# Revit family: Casement_34_B_Top_Hung_Standard
name_source: partatom
category: Windows
revit_build: Autodesk Revit 2014 (Build: 20130308_1515(x64)
units: mm (PartAtom-declared; Revit-internal decimal feet)

## types (6) — shared parameters
Aluminium Thickness = 1 mm  [stored 0.00328084 ft]
Area Pane Left = 0.23 m²
Bead SG Gap = 13 mm  [stored 0.0426509 ft]
Bottom Hung = No
Casement Dimension = 34 mm
Clearvue Insulated LowE SHGC Value = 0.467
Custom Sash Width = 554 mm  [stored 1.81759 ft]
Custom Window Height = 590 mm  [stored 1.9357 ft]
DG Extrusion Start = 7 mm  [stored 0.0229659 ft]
DG Gasket Finish = Double Glazing Gasket Material
DG Thickness Calc = 4 mm  [stored 0.0131234 ft]
Default Sill Height = 800 mm  [stored 2.62467 ft]
Depth Bead = 20 mm  [stored 0.0656168 ft]
Depth Mullion = 35 mm
Description = Window 34mm, Type B top hung
Frame Center Offset = 17 mm
Height = 590 mm  [stored 1.9357 ft]
Height Panel 4 = 530 mm  [stored 1.73885 ft]
Height Sash = 514 mm
Height Sash Opening = 544 mm  [stored 1.78478 ft]
Length Mullion = 590 mm  [stored 1.9357 ft]
Limit Fixed Panel Width Max = 1500 mm  [stored 4.92126 ft]
Limit Fixed Panel Width Min = 200 mm  [stored 0.656168 ft]
Limit Sash Height Max = 900 mm  [stored 2.95276 ft]
Limit Sash Height Min = 300 mm  [stored 0.984252 ft]
Limit Sash Width Max = 1200 mm
Limit Sash Width Min = 300 mm  [stored 0.984252 ft]
Limit Window Height Max = 946 mm  [stored 3.10367 ft]
Limit Window Height Min = 346 mm
Limit Window Width Max = 2129 mm  [stored 6.98491 ft]
Limit Window Width Min = 829 mm  [stored 2.71982 ft]
Manufacturer = Crealco
Max System DG One Piece Thickness = 4 mm  [stored 0.0131234 ft]
Max System DG Unit Thickness = 20 mm  [stored 0.0656168 ft]
Model = Casement 34
Mullion Depth Windload Based = 35 mm
Offset Bead SG Center Reversed = 17 mm
Offset Mullion Left = 569 mm  [stored 1.8668 ft]
Offset Panel 4 Left = 599 mm  [stored 1.96522 ft]
Offset Sash Left = 23 mm  [stored 0.0754593 ft]
Offset Sash Top = 23 mm  [stored 0.0754593 ft]
Offset Window Exterior = 17 mm
SG Gasket Thickness = 6 mm  [stored 0.019685 ft]
Sash Center Offset = 14 mm  [stored 0.0459318 ft]
Sash Overlap = 7 mm  [stored 0.0229659 ft]
Sash Spacing Inner = 8 mm  [stored 0.0262467 ft]
Top Hung = Yes
URL = http://www.crealco.co.za
Wall Closure = By host
Width Bead = 15 mm  [stored 0.0492126 ft]
Width Panel 1 = 539 mm  [stored 1.76837 ft]
Width Profile = 30 mm  [stored 0.0984252 ft]
Width Sash = 524 mm  [stored 1.71916 ft]
Width Sash Opening = 554 mm  [stored 1.81759 ft]
zero-valued in all types: Window Exterior Offset

## per-type parameters (varying)
| type | Area Pane Right | Clearvue Insulated LowE U Value | Clearvue Insulated SHGC Value | Clearvue Insulated U Value | Clearvue SHGC Value | Clearvue U Value | Custom Windload | Custom Window Width | Energy Advantage SHGC Value | Energy Advantage U Value | Intruderprufe LowE SHGC Value | Intruderprufe LowE U Value | Intruderprufe SHGC Value | Intruderprufe U Value | Max Pane Area | Width | Width Panel 4 | Windload Design |
| 34-1206T-1000Pa | 0.29 m² | 3.65 | 0.513 | 4.2 | 0.576 | 6.13 | 1000 mm  [stored 3.28084 ft] | 1190 mm  [stored 3.9042 ft] | 0.516 | 4.77 | 0.484 | 4.54 | 0.544 | 6.06 | 0.29 m² | 1190 mm  [stored 3.9042 ft] | 561 mm  [stored 1.84055 ft] | 1000 mm  [stored 3.28084 ft] |
| 34-1206T-1500Pa | 0.29 m² | 3.65 | 0.513 | 4.2 | 0.576 | 6.13 | 1500 mm  [stored 4.92126 ft] | 1190 mm  [stored 3.9042 ft] | 0.516 | 4.77 | 0.484 | 4.54 | 0.544 | 6.06 | 0.29 m² | 1190 mm  [stored 3.9042 ft] | 561 mm  [stored 1.84055 ft] | 1500 mm  [stored 4.92126 ft] |
| 34-1206T-2000Pa | 0.29 m² | 3.65 | 0.513 | 4.2 | 0.576 | 6.13 | 2000 mm  [stored 6.56168 ft] | 1190 mm  [stored 3.9042 ft] | 0.516 | 4.77 | 0.484 | 4.54 | 0.544 | 6.06 | 0.29 m² | 1190 mm  [stored 3.9042 ft] | 561 mm  [stored 1.84055 ft] | 2000 mm  [stored 6.56168 ft] |
| 34-1506T-1000Pa | 0.44 m² | 3.68 | 0.512 | 4.21 | 0.575 | 6.15 | 1000 mm  [stored 3.28084 ft] | 1490 mm  [stored 4.88845 ft] | 0.515 | 4.8 | 0.483 | 4.52 | 0.543 | 6.11 | 0.44 m² | 1490 mm  [stored 4.88845 ft] | 861 mm | 1000 mm  [stored 3.28084 ft] |
| 34-1506T-1500Pa | 0.44 m² | 3.68 | 0.512 | 4.21 | 0.575 | 6.15 | 1500 mm  [stored 4.92126 ft] | 1490 mm  [stored 4.88845 ft] | 0.515 | 4.8 | 0.483 | 4.52 | 0.543 | 6.11 | 0.44 m² | 1490 mm  [stored 4.88845 ft] | 861 mm | 1500 mm  [stored 4.92126 ft] |
| 34-1506T-2000Pa | 0.44 m² | 3.68 | 0.512 | 4.21 | 0.575 | 6.15 | 2000 mm  [stored 6.56168 ft] | 1490 mm  [stored 4.88845 ft] | 0.515 | 4.8 | 0.483 | 4.52 | 0.543 | 6.11 | 0.44 m² | 1490 mm  [stored 4.88845 ft] | 861 mm | 2000 mm  [stored 6.56168 ft] |

note: [stored X ft] marks values corroborated as IEEE doubles in the binary element streams (Revit-internal decimal feet)

## geometry (parser evidence)
native form markers: Extrusion x1, Sweep x29
no freeform markers — native parametric forms only
